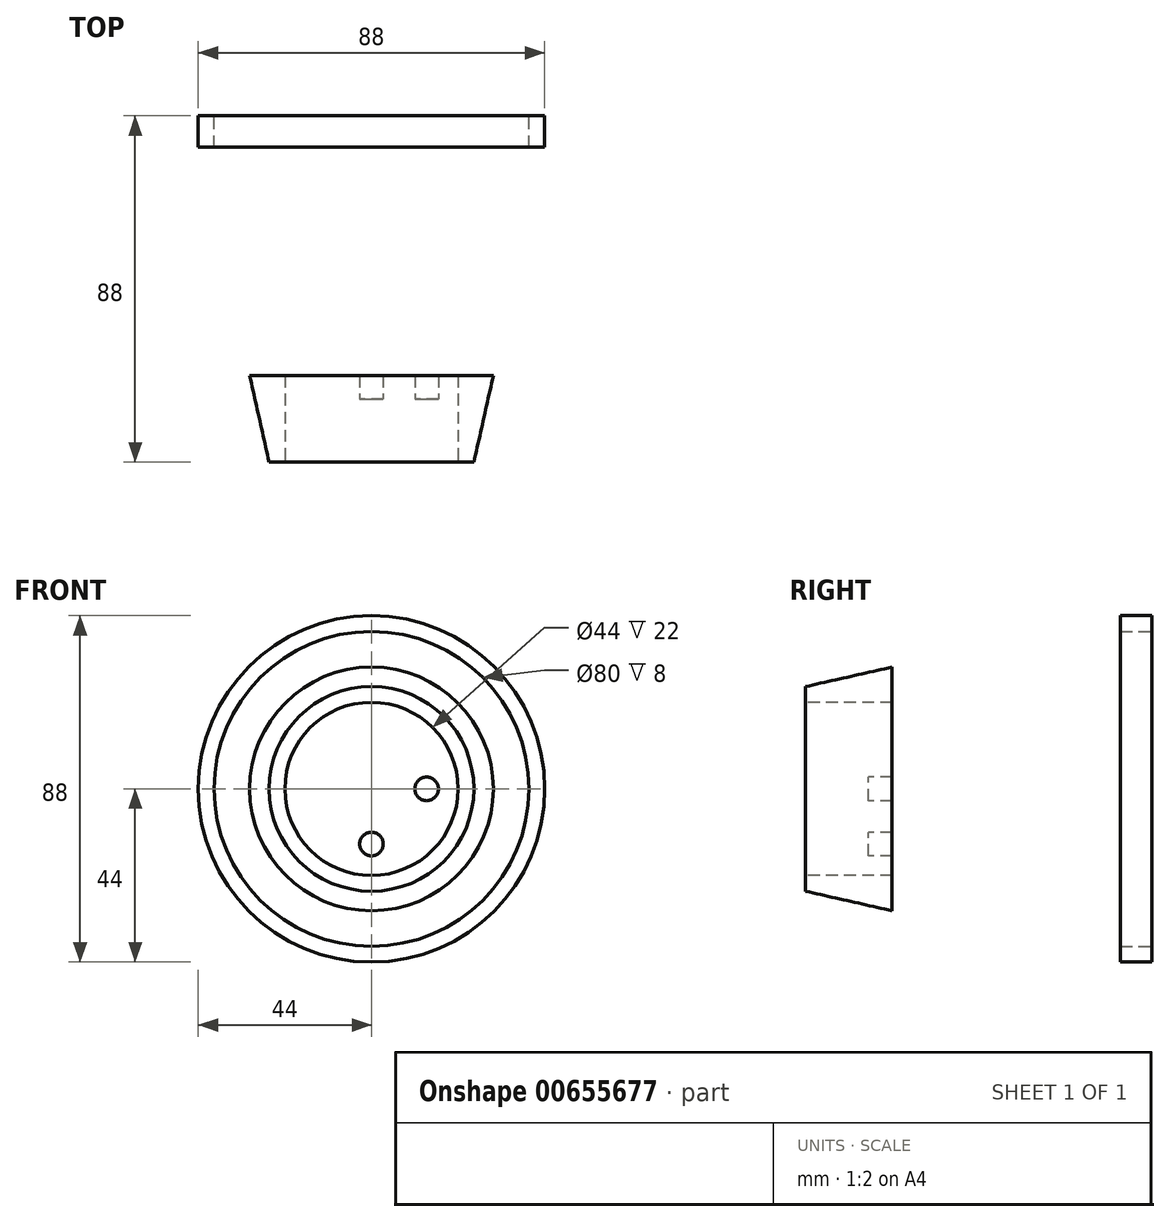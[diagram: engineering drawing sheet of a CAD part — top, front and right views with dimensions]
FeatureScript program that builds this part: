
annotation { "Feature Type Name" : "Feature", "Feature Type Description" : "" }
export const myFeature = defineFeature(function(context is Context, id is Id, definition is map)
    precondition{}
    {
        {
            var Q0;
            Q0=qCreatedBy(makeId("Front.planeOp"),FACE);
            var sketch = newSketch(context, id + "F0", { "sketchPlane" : qUnion([Q0])});
            skCircle(sketch, "E0", {"center": v(0, 0) * mm, "radius": 26 * mm});
            skSolve(sketch);
        }
        {
            var Q0;
            Q0 = qSketchRegion(id + "F0", true);
            var Q1;
            Q1=makeQuery(id+"F0.imprint","IMPRINT",FACE,{"disambiguationData":[TD([[makeQuery(id+"F0.imprint","IMPRINT",EDGE,{"derivedFrom":sQuery(id+"F0.wireOp",EDGE,"CLodPPDq-CJ9s-QT9o-I0qe-w8wCz7oj4dkj")}),1.0]])]});
            extrude(context, id + "F1", {"entities" : qUnion([Q0, Q1]), "oppositeDirection" : true, "depth" : 22 * mm, "offsetDistance" : 25 * mm});
        }
        {
            var Q0;
            Q0=qCreatedBy(makeId("Top.planeOp"),FACE);
            var sketch = newSketch(context, id + "F2", { "sketchPlane" : qUnion([Q0])});
            skLineSegment(sketch, "E1", {"start": v(0, 0) * mm, "end": v(-26, 0) * mm});
            skLineSegment(sketch, "E2", {"start": v(0, 0) * mm, "end": v(0, 80) * mm});
            skLineSegment(sketch, "E3", {"start": v(0, 80) * mm, "end": v(-44, 80) * mm});
            skArc(sketch, "E4", {"start": v(-44, 80) * mm, "mid": v(-35, 40) * mm, "end": v(-26, 0) * mm});
            skLineSegment(sketch, "E5", {"start": v(0, 0) * mm, "end": v(0, 22) * mm});
            skLineSegment(sketch, "E6", {"start": v(0, 22) * mm, "end": v(-30.96, 22) * mm});
            skLineSegment(sketch, "E7", {"start": v(-26, 0) * mm, "end": v(-26, 22) * mm});
            skLineSegment(sketch, "E8", {"start": v(0, 80) * mm, "end": v(0, 88) * mm});
            skLineSegment(sketch, "E9", {"start": v(0, 88) * mm, "end": v(-44, 88) * mm});
            skLineSegment(sketch, "E10", {"start": v(-44, 88) * mm, "end": v(-44, 80) * mm});
            skArc(sketch, "E11.MirrorCS", {"start": v(44, 80) * mm, "mid": v(35, 40) * mm, "end": v(26, 0) * mm});
            skSolve(sketch);
        }
        {
            var Q0;
            Q0=makeQuery(id+"F2.imprint","IMPRINT",FACE,{"disambiguationData":[TD([[makeQuery(id+"F2.imprint","IMPRINT",EDGE,{"derivedFrom":sQuery(id+"F2.wireOp",EDGE,"E2")}),1.0]])]});
            var Q1;
            Q1=sQuery(id+"F2.wireOp",EDGE,"E2");
            revolve(context, id + "F3", {"operationType" : NewBodyOperationType.ADD, "entities" : qUnion([Q0]), "axis" : qUnion([Q1]), "revolveType" : RevolveType.FULL});
        }
        {
            var Q0;
            Q0=qCreatedBy(makeId("Top.planeOp"),FACE);
            var sketch = newSketch(context, id + "F4", { "sketchPlane" : qUnion([Q0])});
            skLineSegment(sketch, "E12", {"start": v(0, 0) * mm, "end": v(0, 88) * mm});
            skLineSegment(sketch, "E13", {"start": v(0, 88) * mm, "end": v(-44, 88) * mm});
            skLineSegment(sketch, "E14", {"start": v(-44, 88) * mm, "end": v(-44, 80) * mm});
            skLineSegment(sketch, "E15", {"start": v(-44, 80) * mm, "end": v(0, 80) * mm});
            skSolve(sketch);
        }
        {
            var Q0;
            {var subQ0=sQuery(id+"F4.wireOp",EDGE,"E13");Q0=makeQuery(id+"F4.imprint","IMPRINT",FACE,{"disambiguationData":[TD([[makeQuery(id+"F4.imprint","IMPRINT",EDGE,{"derivedFrom":subQ0}),1.0]])]});}
            var Q1;
            Q1=sQuery(id+"F4.wireOp",EDGE,"E14");
            var Q2;
            Q2=sQuery(id+"F4.wireOp",EDGE,"E13");
            var Q3;
            Q3=sQuery(id+"F4.wireOp",EDGE,"E12");
            revolve(context, id + "F5", {"operationType" : NewBodyOperationType.ADD, "entities" : qUnion([Q0]), "surfaceEntities" : qUnion([Q1, Q2]), "axis" : qUnion([Q3]), "revolveType" : RevolveType.FULL});
        }
        {
            var Q0;
            {var subQ0=sQuery(id+"F2.wireOp",EDGE,"E7");Q0=makeQuery(id+"F2.imprint","IMPRINT",FACE,{"disambiguationData":[TD([[makeQuery(id+"F2.imprint","IMPRINT",EDGE,{"derivedFrom":subQ0}),1.0]])]});}
            var Q1;
            Q1=makeQuery(id+"F1.opExtrude","SWEPT_FACE",FACE,{"disambiguationData":[OSD([sQuery(id+"F0.wireOp",EDGE,"E0")])]});
            revolve(context, id + "F6", {"operationType" : NewBodyOperationType.ADD, "entities" : qUnion([Q0]), "axis" : qUnion([Q1]), "revolveType" : RevolveType.FULL});
        }
        {
            var Q0;
            Q0=makeQuery(id+"F1.opExtrude","CAP_FACE",FACE,{"disambiguationData":[OSD([sQuery(id+"F0.wireOp",EDGE,"E0")])],"isStart":true});
            var sketch = newSketch(context, id + "F7", { "sketchPlane" : qUnion([Q0])});
            skCircle(sketch, "E16", {"center": v(0, 0) * mm, "radius": 22 * mm});
            skSolve(sketch);
        }
        {
            var Q0;
            Q0 = qSketchRegion(id + "F7", true);
            extrude(context, id + "F8", {"entities" : qUnion([Q0]), "operationType" : NewBodyOperationType.REMOVE, "oppositeDirection" : true, "depth" : 16 * mm, "offsetDistance" : 25 * mm});
        }
        {
            var Q0;
            Q0=makeQuery(id+"F5.opRevolve","SWEPT_FACE",FACE,{"disambiguationData":[OSD([sQuery(id+"F4.wireOp",EDGE,"E13")])]});
            var sketch = newSketch(context, id + "F9", { "sketchPlane" : qUnion([Q0])});
            skCircle(sketch, "E17", {"center": v(0, 0) * mm, "radius": 40 * mm});
            skSolve(sketch);
        }
        {
            var Q0;
            Q0 = qSketchRegion(id + "F9", true);
            extrude(context, id + "F10", {"entities" : qUnion([Q0]), "operationType" : NewBodyOperationType.REMOVE, "oppositeDirection" : true, "depth" : 8 * mm, "offsetDistance" : 25 * mm});
        }
        {
            var Q0;
            Q0=makeQuery(id+"F8.boolean.opBoolean","COPY",FACE,{"derivedFrom":makeQuery(id+"F8.opExtrude","CAP_FACE",FACE,{"disambiguationData":[OSD([sQuery(id+"F7.wireOp",EDGE,"E16")])],"isStart":false})});
            var sketch = newSketch(context, id + "F11", { "sketchPlane" : qUnion([Q0])});
            skCircle(sketch, "E18", {"center": v(0, 0) * mm, "radius": 6 * mm});
            skSolve(sketch);
        }
        {
            var Q0;
            Q0 = qSketchRegion(id + "F11", true);
            extrude(context, id + "F12", {"entities" : qUnion([Q0]), "operationType" : NewBodyOperationType.REMOVE, "oppositeDirection" : true, "depth" : 88 * mm, "offsetDistance" : 25 * mm});
        }
        {
            var Q0;
            Q0=makeQuery(id+"F8.boolean.opBoolean","COPY",FACE,{"derivedFrom":makeQuery(id+"F8.opExtrude","CAP_FACE",FACE,{"disambiguationData":[OSD([sQuery(id+"F7.wireOp",EDGE,"E16")])],"isStart":false})});
            var sketch = newSketch(context, id + "F13", { "sketchPlane" : qUnion([Q0])});
            skCircle(sketch, "E19", {"center": v(0, 0) * mm, "radius": 14 * mm});
            skCircle(sketch, "E20", {"center": v(-14, 0) * mm, "radius": 3 * mm});
            skCircle(sketch, "E21", {"center": v(0, 14) * mm, "radius": 3 * mm});
            skCircle(sketch, "E22", {"center": v(0, -14) * mm, "radius": 3 * mm});
            skCircle(sketch, "E23", {"center": v(14, 0) * mm, "radius": 3 * mm});
            skSolve(sketch);
        }
        {
            var Q0;
            Q0=makeQuery(id+"F13.imprint","IMPRINT",FACE,{"disambiguationData":[TD([[makeQuery(id+"F13.imprint","IMPRINT",EDGE,{"derivedFrom":makeQuery(id+"F12.boolean.opBoolean","COPY",EDGE,{"derivedFrom":makeQuery(id+"F12.opExtrude","CAP_EDGE",EDGE,{"disambiguationData":[OSD([sQuery(id+"F11.wireOp",EDGE,"E18")])],"isStart":true})})}),1.0]])]});
            var Q1;
            {var subQ0=sQuery(id+"F13.wireOp",EDGE,"E21");var subQ1=sQuery(id+"F13.wireOp",EDGE,"E19");var subQ2=makeQuery(id+"F13.imprint","INTERSECT",VERTEX,{"disambiguationData":[OD(0.0)],"derivedFrom":[subQ1,subQ0]});Q1=makeQuery(id+"F13.imprint","IMPRINT",FACE,{"disambiguationData":[TD([[makeQuery(id+"F13.imprint","IMPRINT",EDGE,{"disambiguationData":[TD([[subQ2,-1.0]])],"derivedFrom":subQ1}),1.0]])]});}
            var Q2;
            {var subQ0=sQuery(id+"F13.wireOp",EDGE,"E21");var subQ1=sQuery(id+"F13.wireOp",EDGE,"E19");var subQ2=makeQuery(id+"F13.imprint","INTERSECT",VERTEX,{"disambiguationData":[OD(0.0)],"derivedFrom":[subQ1,subQ0]});Q2=makeQuery(id+"F13.imprint","IMPRINT",FACE,{"disambiguationData":[TD([[makeQuery(id+"F13.imprint","IMPRINT",EDGE,{"disambiguationData":[TD([[subQ2,-1.0]])],"derivedFrom":subQ1}),-1.0]])]});}
            var Q3;
            {var subQ0=sQuery(id+"F13.wireOp",EDGE,"E20");var subQ1=sQuery(id+"F13.wireOp",EDGE,"E19");var subQ2=makeQuery(id+"F13.imprint","INTERSECT",VERTEX,{"disambiguationData":[OD(0.0)],"derivedFrom":[subQ1,subQ0]});Q3=makeQuery(id+"F13.imprint","IMPRINT",FACE,{"disambiguationData":[TD([[makeQuery(id+"F13.imprint","IMPRINT",EDGE,{"disambiguationData":[TD([[subQ2,-1.0]])],"derivedFrom":subQ1}),-1.0]])]});}
            var Q4;
            {var subQ0=sQuery(id+"F13.wireOp",EDGE,"E20");var subQ1=sQuery(id+"F13.wireOp",EDGE,"E19");var subQ2=makeQuery(id+"F13.imprint","INTERSECT",VERTEX,{"disambiguationData":[OD(0.0)],"derivedFrom":[subQ1,subQ0]});Q4=makeQuery(id+"F13.imprint","IMPRINT",FACE,{"disambiguationData":[TD([[makeQuery(id+"F13.imprint","IMPRINT",EDGE,{"disambiguationData":[TD([[subQ2,-1.0]])],"derivedFrom":subQ1}),1.0]])]});}
            var Q5;
            {var subQ0=sQuery(id+"F13.wireOp",EDGE,"E22");var subQ1=sQuery(id+"F13.wireOp",EDGE,"E19");var subQ2=makeQuery(id+"F13.imprint","INTERSECT",VERTEX,{"disambiguationData":[OD(0.0)],"derivedFrom":[subQ1,subQ0]});Q5=makeQuery(id+"F13.imprint","IMPRINT",FACE,{"disambiguationData":[TD([[makeQuery(id+"F13.imprint","IMPRINT",EDGE,{"disambiguationData":[TD([[subQ2,-1.0]])],"derivedFrom":subQ1}),1.0]])]});}
            var Q6;
            {var subQ0=sQuery(id+"F13.wireOp",EDGE,"E22");var subQ1=sQuery(id+"F13.wireOp",EDGE,"E19");var subQ2=makeQuery(id+"F13.imprint","INTERSECT",VERTEX,{"disambiguationData":[OD(0.0)],"derivedFrom":[subQ1,subQ0]});Q6=makeQuery(id+"F13.imprint","IMPRINT",FACE,{"disambiguationData":[TD([[makeQuery(id+"F13.imprint","IMPRINT",EDGE,{"disambiguationData":[TD([[subQ2,-1.0]])],"derivedFrom":subQ1}),-1.0]])]});}
            var Q7;
            {var subQ0=sQuery(id+"F13.wireOp",EDGE,"E23");var subQ1=sQuery(id+"F13.wireOp",EDGE,"E19");var subQ2=makeQuery(id+"F13.imprint","INTERSECT",VERTEX,{"disambiguationData":[OD(0.0)],"derivedFrom":[subQ1,subQ0]});Q7=makeQuery(id+"F13.imprint","IMPRINT",FACE,{"disambiguationData":[TD([[makeQuery(id+"F13.imprint","IMPRINT",EDGE,{"disambiguationData":[TD([[subQ2,1.0]])],"derivedFrom":subQ1}),1.0]])]});}
            var Q8;
            {var subQ0=sQuery(id+"F13.wireOp",EDGE,"E23");var subQ1=sQuery(id+"F13.wireOp",EDGE,"E19");var subQ2=makeQuery(id+"F13.imprint","INTERSECT",VERTEX,{"disambiguationData":[OD(0.0)],"derivedFrom":[subQ1,subQ0]});Q8=makeQuery(id+"F13.imprint","IMPRINT",FACE,{"disambiguationData":[TD([[makeQuery(id+"F13.imprint","IMPRINT",EDGE,{"disambiguationData":[TD([[subQ2,1.0]])],"derivedFrom":subQ1}),-1.0]])]});}
            extrude(context, id + "F14", {"entities" : qUnion([Q0, Q1, Q2, Q3, Q4, Q5, Q6, Q7, Q8]), "operationType" : NewBodyOperationType.REMOVE, "oppositeDirection" : true, "depth" : 88 * mm, "offsetDistance" : 25 * mm});
        }
    });
